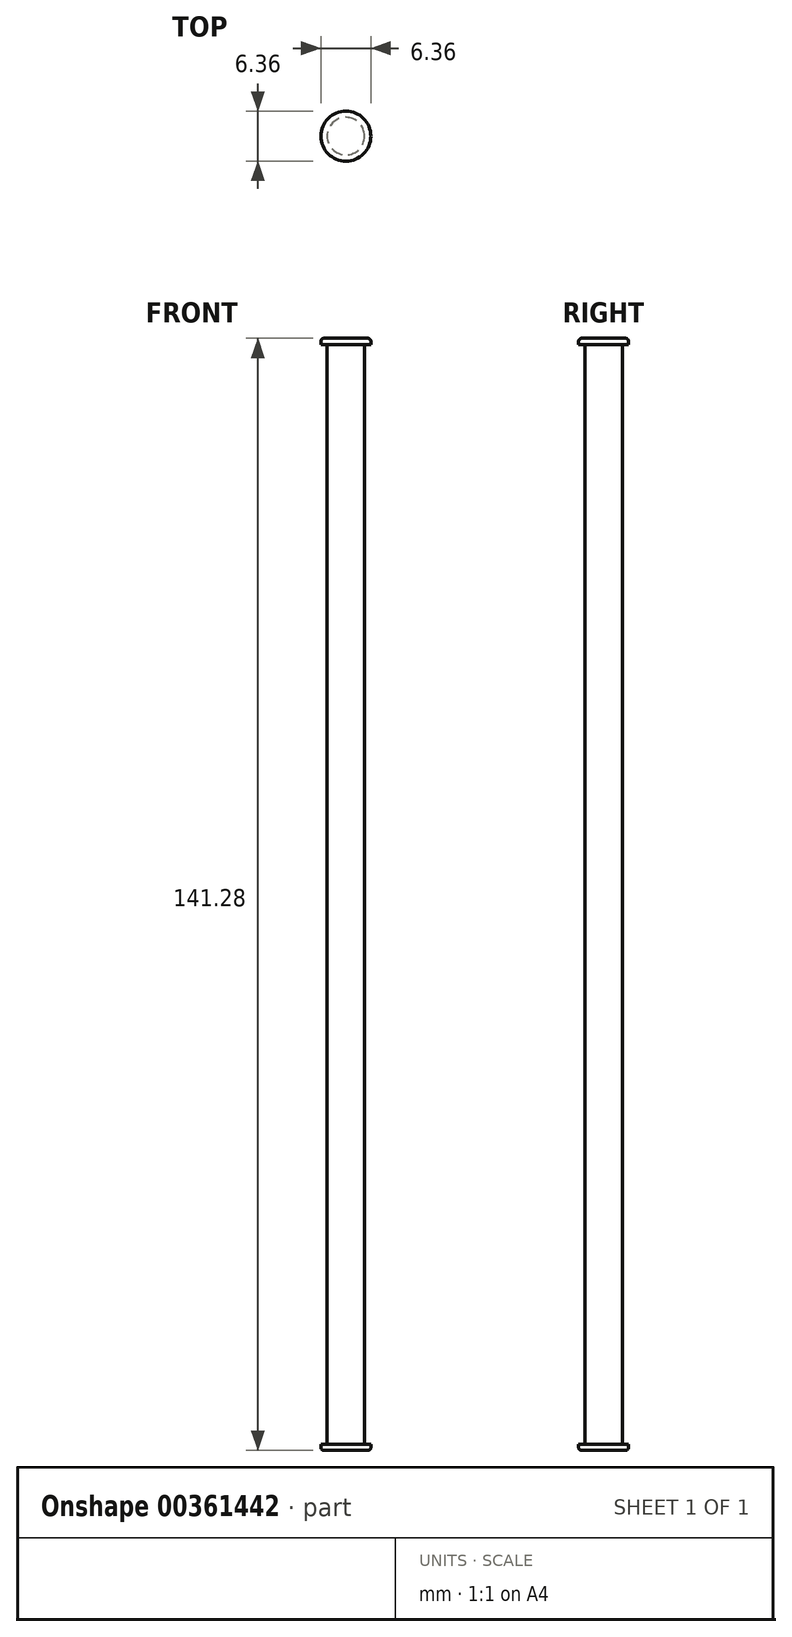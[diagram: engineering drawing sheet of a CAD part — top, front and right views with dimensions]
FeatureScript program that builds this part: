
annotation { "Feature Type Name" : "Feature", "Feature Type Description" : "" }
export const myFeature = defineFeature(function(context is Context, id is Id, definition is map)
    precondition{}
    {
        {
            var Q0;
            Q0=qCreatedBy(makeId("Top.planeOp"),FACE);
            var sketch = newSketch(context, id + "F0", { "sketchPlane" : qUnion([Q0])});
            skCircle(sketch, "E0", {"center": v(0, 0) * mm, "radius": 2.38 * mm});
            skSolve(sketch);
        }
        {
            var Q0;
            Q0=makeQuery(id+"F0.imprint","IMPRINT",FACE,{"disambiguationData":[TD([[makeQuery(id+"F0.imprint","IMPRINT",EDGE,{"derivedFrom":sQuery(id+"F0.wireOp",EDGE,"E0")}),1.0]])]});
            extrude(context, id + "F1", {"entities" : qUnion([Q0]), "depth" : 69.85 * mm});
        }
        {
            var Q0;
            Q0=makeQuery(id+"F1.opExtrude","CAP_FACE",FACE,{"disambiguationData":[OSD([sQuery(id+"F0.wireOp",EDGE,"E0")])],"isStart":true});
            var sketch = newSketch(context, id + "F2", { "sketchPlane" : qUnion([Q0])});
            skCircle(sketch, "E1", {"center": v(0, 0) * mm, "radius": 3.18 * mm});
            skSolve(sketch);
        }
        {
            var Q0;
            Q0 = qSketchRegion(id + "F2", true);
            extrude(context, id + "F3", {"entities" : qUnion([Q0]), "operationType" : NewBodyOperationType.ADD, "depth" : 0.8 * mm});
        }
        {
            var Q0;
            Q0=makeQuery(id+"F3.opExtrude","CAP_EDGE",EDGE,{"disambiguationData":[OSD([sQuery(id+"F2.wireOp",EDGE,"E1")])],"isStart":false});
            fillet(context, id + "F4", {"entities" : qUnion([Q0]), "radius" : 0.4 * mm, "tangentPropagation" : true, "allowEdgeOverflow" : false});
        }
        {
            var Q0;
            Q0=makeQuery(id+"F1.opExtrude","SWEPT_BODY",BODY,{"disambiguationData":[OSD([sQuery(id+"F0.wireOp",EDGE,"E0")])]});
            var Q1;
            Q1=makeQuery(id+"F1.opExtrude","CAP_FACE",FACE,{"disambiguationData":[OSD([sQuery(id+"F0.wireOp",EDGE,"E0")])],"isStart":false});
            mirror(context, id + "F5", {"operationType" : NewBodyOperationType.ADD, "entities" : qUnion([Q0]), "mirrorPlane" : qUnion([Q1])});
        }
    });
